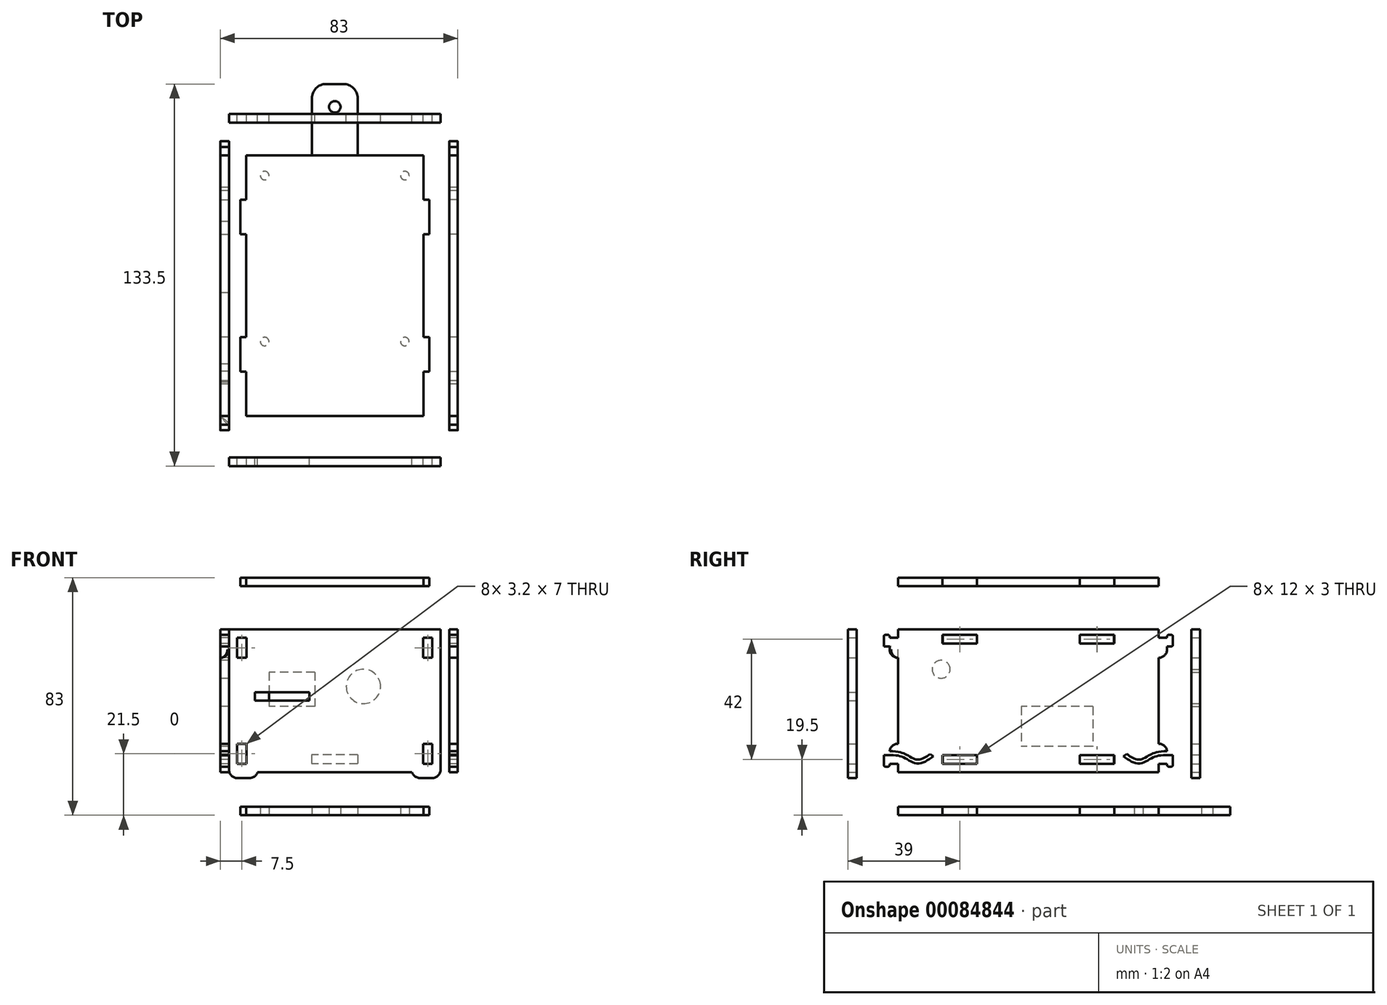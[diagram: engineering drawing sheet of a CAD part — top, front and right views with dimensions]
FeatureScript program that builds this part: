
annotation { "Feature Type Name" : "Feature", "Feature Type Description" : "" }
export const myFeature = defineFeature(function(context is Context, id is Id, definition is map)
    precondition{}
    {
        {
            var Q0;
            Q0=qCreatedBy(makeId("Top.planeOp"),FACE);
            cPlane(context, id + "F0", {"entities" : qUnion([Q0]), "cplaneType" : CPlaneType.OFFSET, "offset" : 40 * mm, "oppositeDirection" : true, "width" : 150 * mm, "height" : 150 * mm});
        }
        {
            var Q0;
            Q0=qCreatedBy(id+"F0.planeOp",FACE);
            var sketch = newSketch(context, id + "F1", { "sketchPlane" : qUnion([Q0])});
            skLineSegment(sketch, "E0", {"start": v(31, 45.5) * mm, "end": v(31, 30) * mm});
            skLineSegment(sketch, "E1", {"start": v(31, 30) * mm, "end": v(33, 30) * mm});
            skLineSegment(sketch, "E2", {"start": v(33, 30) * mm, "end": v(33, 18) * mm});
            skLineSegment(sketch, "E3", {"start": v(33, 18) * mm, "end": v(31, 18) * mm});
            skLineSegment(sketch, "E4", {"start": v(31, 18) * mm, "end": v(31, -18) * mm});
            skLineSegment(sketch, "E5", {"start": v(31, -18) * mm, "end": v(33, -18) * mm});
            skLineSegment(sketch, "E6", {"start": v(33, -18) * mm, "end": v(33, -30) * mm});
            skLineSegment(sketch, "E7", {"start": v(33, -30) * mm, "end": v(31, -30) * mm});
            skLineSegment(sketch, "E8", {"start": v(31, -30) * mm, "end": v(31, -45.5) * mm});
            skLineSegment(sketch, "E9", {"start": v(31, -45.5) * mm, "end": v(0, -45.5) * mm});
            skLineSegment(sketch, "E10", {"start": v(0, -45.5) * mm, "end": v(0, 45.5) * mm, "construction": true});
            skPoint(sketch, "E11", {"position": v(0, 0) * mm});
            skLineSegment(sketch, "E12.MirrorCS", {"start": v(-31, -18) * mm, "end": v(-33, -18) * mm});
            skLineSegment(sketch, "E13.MirrorCS", {"start": v(-33, -18) * mm, "end": v(-33, -30) * mm});
            skLineSegment(sketch, "E14.MirrorCS", {"start": v(-33, -30) * mm, "end": v(-31, -30) * mm});
            skLineSegment(sketch, "E15.MirrorCS", {"start": v(-31, -30) * mm, "end": v(-31, -45.5) * mm});
            skLineSegment(sketch, "E16.MirrorCS", {"start": v(-31, -45.5) * mm, "end": v(0, -45.5) * mm});
            skLineSegment(sketch, "E17.MirrorCS", {"start": v(-31, 18) * mm, "end": v(-31, -18) * mm});
            skLineSegment(sketch, "E18.MirrorCS", {"start": v(-33, 18) * mm, "end": v(-31, 18) * mm});
            skLineSegment(sketch, "E19.MirrorCS", {"start": v(-33, 30) * mm, "end": v(-33, 18) * mm});
            skLineSegment(sketch, "E20.MirrorCS", {"start": v(-31, 30) * mm, "end": v(-33, 30) * mm});
            skLineSegment(sketch, "E21.MirrorCS", {"start": v(-31, 45.5) * mm, "end": v(-31, 30) * mm});
            skCircle(sketch, "E22", {"center": v(24.5, 38.5) * mm, "radius": 1.5 * mm});
            skCircle(sketch, "E23.0.1.0", {"center": v(24.5, -19.5) * mm, "radius": 1.5 * mm});
            skCircle(sketch, "E23.1.0.0", {"center": v(-24.5, 38.5) * mm, "radius": 1.5 * mm});
            skCircle(sketch, "E23.1.1.0", {"center": v(-24.5, -19.5) * mm, "radius": 1.5 * mm});
            skLineSegment(sketch, "E23.direction1", {"start": v(24.5, 38.5) * mm, "end": v(-24.5, 38.5) * mm, "construction": true});
            skLineSegment(sketch, "E23.direction2", {"start": v(24.5, 38.5) * mm, "end": v(24.5, -19.5) * mm, "construction": true});
            skLineSegment(sketch, "E24", {"start": v(24.5, -19.5) * mm, "end": v(-24.5, -19.5) * mm, "construction": true});
            skPoint(sketch, "E25", {"position": v(0, -19.5) * mm});
            skLineSegment(sketch, "E26", {"start": v(31, 45.5) * mm, "end": v(8, 45.5) * mm});
            skLineSegment(sketch, "E27", {"start": v(8, 45.5) * mm, "end": v(8, 65.5) * mm});
            skLineSegment(sketch, "E28", {"start": v(3, 70.5) * mm, "end": v(0, 70.5) * mm});
            skLineSegment(sketch, "E29.MirrorCS", {"start": v(-31, 45.5) * mm, "end": v(-8, 45.5) * mm});
            skLineSegment(sketch, "E30.MirrorCS", {"start": v(-8, 45.5) * mm, "end": v(-8, 65.5) * mm});
            skLineSegment(sketch, "E31.MirrorCS", {"start": v(-3, 70.5) * mm, "end": v(0, 70.5) * mm});
            skCircle(sketch, "E32", {"center": v(0, 62.5) * mm, "radius": 2 * mm});
            skPoint(sketch, "E33.visualSharp", {"position": v(8, 70.5) * mm});
            skArc(sketch, "E33.filletArc", {"start": v(8, 65.5) * mm, "mid": v(6.54, 69.04) * mm, "end": v(3, 70.5) * mm});
            skPoint(sketch, "E34.visualSharp", {"position": v(-8, 70.5) * mm});
            skArc(sketch, "E34.filletArc", {"start": v(-3, 70.5) * mm, "mid": v(-6.54, 69.04) * mm, "end": v(-8, 65.5) * mm});
            skSolve(sketch);
        }
        {
            var Q0;
            Q0=qSketchRegion(id+"F1",true);
            extrude(context, id + "F2", {"entities" : qUnion([Q0]), "depth" : 3 * mm});
        }
        {
            var Q0;
            Q0=qCreatedBy(makeId("Top.planeOp"),FACE);
            cPlane(context, id + "F3", {"entities" : qUnion([Q0]), "cplaneType" : CPlaneType.OFFSET, "offset" : 40 * mm, "width" : 150 * mm, "height" : 150 * mm});
        }
        {
            var Q0;
            Q0=qCreatedBy(id+"F3.planeOp",FACE);
            var sketch = newSketch(context, id + "F4", { "sketchPlane" : qUnion([Q0])});
            skLineSegment(sketch, "E35", {"start": v(0, 45.5) * mm, "end": v(31, 45.5) * mm});
            skLineSegment(sketch, "E36", {"start": v(31, 45.5) * mm, "end": v(31, 30) * mm});
            skLineSegment(sketch, "E37", {"start": v(31, 30) * mm, "end": v(33, 30) * mm});
            skLineSegment(sketch, "E38", {"start": v(33, 30) * mm, "end": v(33, 18) * mm});
            skLineSegment(sketch, "E39", {"start": v(33, 18) * mm, "end": v(31, 18) * mm});
            skLineSegment(sketch, "E40", {"start": v(31, 18) * mm, "end": v(31, -18) * mm});
            skLineSegment(sketch, "E41", {"start": v(31, -18) * mm, "end": v(33, -18) * mm});
            skLineSegment(sketch, "E42", {"start": v(33, -18) * mm, "end": v(33, -30) * mm});
            skLineSegment(sketch, "E43", {"start": v(33, -30) * mm, "end": v(31, -30) * mm});
            skLineSegment(sketch, "E44", {"start": v(31, -30) * mm, "end": v(31, -45.5) * mm});
            skLineSegment(sketch, "E45", {"start": v(31, -45.5) * mm, "end": v(0, -45.5) * mm});
            skLineSegment(sketch, "E46.MirrorCS", {"start": v(-31, -18) * mm, "end": v(-33, -18) * mm});
            skLineSegment(sketch, "E47.MirrorCS", {"start": v(-33, -18) * mm, "end": v(-33, -30) * mm});
            skLineSegment(sketch, "E48.MirrorCS", {"start": v(-33, -30) * mm, "end": v(-31, -30) * mm});
            skLineSegment(sketch, "E49.MirrorCS", {"start": v(-31, -30) * mm, "end": v(-31, -45.5) * mm});
            skLineSegment(sketch, "E50.MirrorCS", {"start": v(-31, -45.5) * mm, "end": v(0, -45.5) * mm});
            skLineSegment(sketch, "E51.MirrorCS", {"start": v(-31, 18) * mm, "end": v(-31, -18) * mm});
            skLineSegment(sketch, "E52.MirrorCS", {"start": v(-33, 18) * mm, "end": v(-31, 18) * mm});
            skLineSegment(sketch, "E53.MirrorCS", {"start": v(-33, 30) * mm, "end": v(-33, 18) * mm});
            skLineSegment(sketch, "E54.MirrorCS", {"start": v(-31, 30) * mm, "end": v(-33, 30) * mm});
            skLineSegment(sketch, "E55.MirrorCS", {"start": v(-31, 45.5) * mm, "end": v(-31, 30) * mm});
            skLineSegment(sketch, "E56.MirrorCS", {"start": v(0, 45.5) * mm, "end": v(-31, 45.5) * mm});
            skLineSegment(sketch, "E57", {"start": v(0, 45.5) * mm, "end": v(0, -45.5) * mm, "construction": true});
            skPoint(sketch, "E58", {"position": v(0, 0) * mm});
            skSolve(sketch);
        }
        {
            var Q0;
            Q0=makeQuery(id+"F4.imprint","IMPRINT",FACE,{"disambiguationData":[TD([[makeQuery(id+"F4.imprint","IMPRINT",EDGE,{"derivedFrom":sQuery(id+"F4.wireOp",EDGE,"E35")}),-1.0]])]});
            extrude(context, id + "F5", {"entities" : qUnion([Q0]), "depth" : 3 * mm});
        }
        {
            var Q0;
            Q0=qCreatedBy(makeId("Right.planeOp"),FACE);
            cPlane(context, id + "F6", {"entities" : qUnion([Q0]), "cplaneType" : CPlaneType.OFFSET, "offset" : 40 * mm, "oppositeDirection" : true, "width" : 150 * mm, "height" : 150 * mm});
        }
        {
            var Q0;
            Q0=qCreatedBy(id+"F6.planeOp",FACE);
            var sketch = newSketch(context, id + "F7", { "sketchPlane" : qUnion([Q0])});
            skLineSegment(sketch, "E59.MirrorCS", {"start": v(-48.5, 23) * mm, "end": v(-48.5, 22) * mm});
            skLineSegment(sketch, "E60.MirrorCS", {"start": v(-48.5, -17.6) * mm, "end": v(-48.5, -15) * mm});
            skLineSegment(sketch, "E61.MirrorCS", {"start": v(-48.5, -22) * mm, "end": v(-48.5, -23) * mm});
            skLineSegment(sketch, "E62.MirrorCS", {"start": v(-48.5, -23) * mm, "end": v(-50.5, -23) * mm});
            skLineSegment(sketch, "E63.MirrorCS", {"start": v(-50.5, -23) * mm, "end": v(-50.5, -19) * mm});
            skLineSegment(sketch, "E64.MirrorCS", {"start": v(-48.5, -17.6) * mm, "end": v(-48.5, -22) * mm, "construction": true});
            skLineSegment(sketch, "E65.MirrorCS", {"start": v(-50.5, 23) * mm, "end": v(-48.5, 23) * mm});
            skLineSegment(sketch, "E66.MirrorCS", {"start": v(-33.23, -19.42) * mm, "end": v(-34.37, -18.6) * mm});
            skLineSegment(sketch, "E67.MirrorCS", {"start": v(-48.5, -17.6) * mm, "end": v(-48.65, -17.6) * mm});
            skLineSegment(sketch, "E68.MirrorCS", {"start": v(-45.5, 22) * mm, "end": v(-45.5, 25) * mm});
            skLineSegment(sketch, "E69.MirrorCS", {"start": v(-45.5, -22) * mm, "end": v(-48.5, -22) * mm});
            skLineSegment(sketch, "E70.MirrorCS", {"start": v(-48.5, -15) * mm, "end": v(-45.5, -15) * mm});
            skLineSegment(sketch, "E71.MirrorCS", {"start": v(-45.5, -25) * mm, "end": v(-45.5, -22) * mm});
            skLineSegment(sketch, "E72.MirrorCS", {"start": v(-17.9, -19) * mm, "end": v(-17.9, -22) * mm});
            skLineSegment(sketch, "E73.MirrorCS", {"start": v(-48.5, 22) * mm, "end": v(-45.5, 22) * mm});
            skLineSegment(sketch, "E74.MirrorCS", {"start": v(-48.5, 19) * mm, "end": v(-48.5, 15) * mm});
            skLineSegment(sketch, "E75.MirrorCS", {"start": v(-48.5, 15) * mm, "end": v(-45.5, 15) * mm});
            skLineSegment(sketch, "E76.MirrorCS", {"start": v(-29.9, -19) * mm, "end": v(-29.9, -22) * mm});
            skLineSegment(sketch, "E77.MirrorCS", {"start": v(-48.5, 19) * mm, "end": v(-50.5, 19) * mm});
            skLineSegment(sketch, "E78.MirrorCS", {"start": v(-50.5, 19) * mm, "end": v(-50.5, 23) * mm});
            skFitSpline(sketch, "E79.MirrorCS", {"points": [v(-52.36, -17.56) * mm, v(-51.07, -17.58) * mm, v(-49.38, -17.58) * mm, v(-47.44, -17.63) * mm, v(-46.09, -17.74) * mm, v(-45.02, -17.93) * mm, v(-44.18, -18.16) * mm, v(-43.67, -18.34) * mm, v(-43.26, -18.51) * mm, v(-42.87, -18.7) * mm, v(-42.4, -18.94) * mm, v(-41.88, -19.24) * mm, v(-41.2, -19.63) * mm, v(-40.59, -19.98) * mm, v(-40.01, -20.25) * mm, v(-39.61, -20.4) * mm, v(-39.3, -20.5) * mm, v(-39.06, -20.54) * mm, v(-38.9, -20.55) * mm, v(-38.72, -20.56) * mm, v(-38.47, -20.55) * mm, v(-38.14, -20.5) * mm, v(-37.7, -20.4) * mm, v(-37.1, -20.2) * mm, v(-36.3, -19.82) * mm, v(-35.31, -19.24) * mm, v(-34.68, -18.82) * mm, v(-34.37, -18.6) * mm]});
            skFitSpline(sketch, "E80.MirrorCS", {"points": [v(-50.5, -19) * mm, v(-43.39, -19.86) * mm, v(-38.75, -21.96) * mm, v(-33.23, -19.42) * mm], "startDerivative": vector(31.3, 0.22) * mm, "endDerivative": vector(15, 10.88) * mm});
            skLineSegment(sketch, "E81.MirrorCS", {"start": v(-17.9, -19) * mm, "end": v(-29.9, -19) * mm});
            skLineSegment(sketch, "E82.MirrorCS", {"start": v(-17.9, -22) * mm, "end": v(-29.9, -22) * mm});
            skLineSegment(sketch, "E83.MirrorCS", {"start": v(-45.5, 25) * mm, "end": v(0, 25) * mm});
            skPoint(sketch, "E84.MirrorP", {"position": v(-48.5, -17.6) * mm});
            skLineSegment(sketch, "E85.MirrorCS", {"start": v(-45.5, -15) * mm, "end": v(-45.5, 15) * mm});
            skLineSegment(sketch, "E86.MirrorCS", {"start": v(-45.5, -25) * mm, "end": v(0, -25) * mm});
            skLineSegment(sketch, "E87.MirrorCS", {"start": v(0, 25) * mm, "end": v(0, -25) * mm, "construction": true});
            skPoint(sketch, "E88.MirrorP", {"position": v(-48.65, -17.6) * mm});
            skPoint(sketch, "E89", {"position": v(0, 0) * mm});
            skLineSegment(sketch, "E90.MirrorCS", {"start": v(-17.9, 20) * mm, "end": v(-29.9, 20) * mm});
            skLineSegment(sketch, "E91.MirrorCS", {"start": v(-17.9, 23) * mm, "end": v(-29.9, 23) * mm});
            skLineSegment(sketch, "E92.MirrorCS", {"start": v(-29.9, 20) * mm, "end": v(-29.9, 23) * mm});
            skLineSegment(sketch, "E93.MirrorCS", {"start": v(-17.9, 20) * mm, "end": v(-17.9, 23) * mm});
            skLineSegment(sketch, "E94", {"start": v(-45.5, -15) * mm, "end": v(-45.5, -22) * mm, "construction": true});
            skLineSegment(sketch, "E95.MirrorCS", {"start": v(48.5, -17.6) * mm, "end": v(48.65, -17.6) * mm});
            skLineSegment(sketch, "E96.MirrorCS", {"start": v(33.23, -19.42) * mm, "end": v(34.37, -18.6) * mm});
            skLineSegment(sketch, "E97.MirrorCS", {"start": v(48.5, -23) * mm, "end": v(50.5, -23) * mm});
            skLineSegment(sketch, "E98.MirrorCS", {"start": v(48.5, -22) * mm, "end": v(48.5, -23) * mm});
            skLineSegment(sketch, "E99.MirrorCS", {"start": v(48.5, -17.6) * mm, "end": v(48.5, -22) * mm, "construction": true});
            skLineSegment(sketch, "E100.MirrorCS", {"start": v(50.5, 23) * mm, "end": v(48.5, 23) * mm});
            skLineSegment(sketch, "E101.MirrorCS", {"start": v(45.5, -22) * mm, "end": v(48.5, -22) * mm});
            skLineSegment(sketch, "E102.MirrorCS", {"start": v(48.5, 23) * mm, "end": v(48.5, 22) * mm});
            skLineSegment(sketch, "E103.MirrorCS", {"start": v(50.5, -23) * mm, "end": v(50.5, -19) * mm});
            skLineSegment(sketch, "E104.MirrorCS", {"start": v(48.5, -15) * mm, "end": v(45.5, -15) * mm});
            skLineSegment(sketch, "E105.MirrorCS", {"start": v(45.5, -25) * mm, "end": v(45.5, -22) * mm});
            skLineSegment(sketch, "E106.MirrorCS", {"start": v(45.5, -15) * mm, "end": v(45.5, -22) * mm, "construction": true});
            skLineSegment(sketch, "E107.MirrorCS", {"start": v(45.5, 22) * mm, "end": v(45.5, 25) * mm});
            skLineSegment(sketch, "E108.MirrorCS", {"start": v(48.5, 19) * mm, "end": v(50.5, 19) * mm});
            skLineSegment(sketch, "E109.MirrorCS", {"start": v(50.5, 19) * mm, "end": v(50.5, 23) * mm});
            skLineSegment(sketch, "E110.MirrorCS", {"start": v(48.5, 15) * mm, "end": v(45.5, 15) * mm});
            skLineSegment(sketch, "E111.MirrorCS", {"start": v(17.9, 20) * mm, "end": v(17.9, 23) * mm});
            skLineSegment(sketch, "E112.MirrorCS", {"start": v(48.5, -17.6) * mm, "end": v(48.5, -15) * mm});
            skLineSegment(sketch, "E113.MirrorCS", {"start": v(17.9, -19) * mm, "end": v(17.9, -22) * mm});
            skLineSegment(sketch, "E114.MirrorCS", {"start": v(48.5, 22) * mm, "end": v(45.5, 22) * mm});
            skLineSegment(sketch, "E115.MirrorCS", {"start": v(29.9, 20) * mm, "end": v(29.9, 23) * mm});
            skLineSegment(sketch, "E116.MirrorCS", {"start": v(29.9, -19) * mm, "end": v(29.9, -22) * mm});
            skPoint(sketch, "E117.MirrorP", {"position": v(48.65, -17.6) * mm});
            skFitSpline(sketch, "E118.MirrorCS", {"points": [v(50.5, -19) * mm, v(43.39, -19.86) * mm, v(38.75, -21.96) * mm, v(33.23, -19.42) * mm], "startDerivative": vector(-31.3, 0.22) * mm, "endDerivative": vector(-15, 10.88) * mm});
            skLineSegment(sketch, "E119.MirrorCS", {"start": v(17.9, 20) * mm, "end": v(29.9, 20) * mm});
            skLineSegment(sketch, "E120.MirrorCS", {"start": v(45.5, 25) * mm, "end": v(0, 25) * mm});
            skLineSegment(sketch, "E121.MirrorCS", {"start": v(45.5, -15) * mm, "end": v(45.5, 15) * mm});
            skLineSegment(sketch, "E122.MirrorCS", {"start": v(17.9, -22) * mm, "end": v(29.9, -22) * mm});
            skLineSegment(sketch, "E123.MirrorCS", {"start": v(45.5, -25) * mm, "end": v(0, -25) * mm});
            skLineSegment(sketch, "E124.MirrorCS", {"start": v(17.9, -19) * mm, "end": v(29.9, -19) * mm});
            skLineSegment(sketch, "E125.MirrorCS", {"start": v(17.9, 23) * mm, "end": v(29.9, 23) * mm});
            skFitSpline(sketch, "E126.MirrorCS", {"points": [v(52.36, -17.56) * mm, v(51.07, -17.58) * mm, v(49.38, -17.58) * mm, v(47.44, -17.63) * mm, v(46.09, -17.74) * mm, v(45.02, -17.93) * mm, v(44.18, -18.16) * mm, v(43.67, -18.34) * mm, v(43.26, -18.51) * mm, v(42.87, -18.7) * mm, v(42.4, -18.94) * mm, v(41.88, -19.24) * mm, v(41.2, -19.63) * mm, v(40.59, -19.98) * mm, v(40.01, -20.25) * mm, v(39.61, -20.4) * mm, v(39.3, -20.5) * mm, v(39.06, -20.54) * mm, v(38.9, -20.55) * mm, v(38.72, -20.56) * mm, v(38.47, -20.55) * mm, v(38.14, -20.5) * mm, v(37.7, -20.4) * mm, v(37.1, -20.2) * mm, v(36.3, -19.82) * mm, v(35.31, -19.24) * mm, v(34.68, -18.82) * mm, v(34.37, -18.6) * mm]});
            skPoint(sketch, "E127.MirrorP", {"position": v(48.5, -17.6) * mm});
            skLineSegment(sketch, "E128.MirrorCS", {"start": v(48.5, 19) * mm, "end": v(48.5, 15) * mm});
            skLineSegment(sketch, "E129", {"start": v(38.75, -21.96) * mm, "end": v(38.75, -20.56) * mm, "construction": true});
            skLineSegment(sketch, "E130", {"start": v(43.39, -19.86) * mm, "end": v(43.39, -18.46) * mm, "construction": true});
            skLineSegment(sketch, "E131.bottom", {"start": v(22.5, -2) * mm, "end": v(-2.5, -2) * mm});
            skLineSegment(sketch, "E131.top", {"start": v(22.5, -16) * mm, "end": v(-2.5, -16) * mm});
            skLineSegment(sketch, "E131.left", {"start": v(22.5, -2) * mm, "end": v(22.5, -16) * mm});
            skLineSegment(sketch, "E131.right", {"start": v(-2.5, -2) * mm, "end": v(-2.5, -16) * mm});
            skCircle(sketch, "E132", {"center": v(-30.5, 11) * mm, "radius": 3.15 * mm});
            skLineSegment(sketch, "E133", {"start": v(-17.9, 20) * mm, "end": v(-17.9, -19) * mm, "construction": true});
            skSolve(sketch);
        }
        {
            var Q0;
            Q0=qSketchRegion(id+"F7",true);
            extrude(context, id + "F8", {"entities" : qUnion([Q0]), "depth" : 3 * mm});
        }
        {
            var Q0;
            Q0=qCreatedBy(makeId("Right.planeOp"),FACE);
            cPlane(context, id + "F9", {"entities" : qUnion([Q0]), "cplaneType" : CPlaneType.OFFSET, "offset" : 40 * mm, "width" : 150 * mm, "height" : 150 * mm});
        }
        {
            var Q0;
            Q0=qCreatedBy(id+"F9.planeOp",FACE);
            var sketch = newSketch(context, id + "F10", { "sketchPlane" : qUnion([Q0])});
            skLineSegment(sketch, "E134.MirrorCS", {"start": v(-48.5, 23) * mm, "end": v(-48.5, 22) * mm});
            skLineSegment(sketch, "E135.MirrorCS", {"start": v(-48.5, -17.6) * mm, "end": v(-48.5, -15) * mm});
            skLineSegment(sketch, "E136.MirrorCS", {"start": v(-48.5, -22) * mm, "end": v(-48.5, -23) * mm});
            skLineSegment(sketch, "E137.MirrorCS", {"start": v(-48.5, -23) * mm, "end": v(-50.5, -23) * mm});
            skLineSegment(sketch, "E138.MirrorCS", {"start": v(-50.5, -23) * mm, "end": v(-50.5, -19) * mm});
            skLineSegment(sketch, "E139.MirrorCS", {"start": v(-48.5, -17.6) * mm, "end": v(-48.5, -22) * mm, "construction": true});
            skLineSegment(sketch, "E140.MirrorCS", {"start": v(-50.5, 23) * mm, "end": v(-48.5, 23) * mm});
            skLineSegment(sketch, "E141.MirrorCS", {"start": v(-33.23, -19.42) * mm, "end": v(-34.37, -18.6) * mm});
            skLineSegment(sketch, "E142.MirrorCS", {"start": v(-48.5, -17.6) * mm, "end": v(-48.65, -17.6) * mm});
            skLineSegment(sketch, "E143.MirrorCS", {"start": v(-45.5, 22) * mm, "end": v(-45.5, 25) * mm});
            skLineSegment(sketch, "E144.MirrorCS", {"start": v(-45.5, -22) * mm, "end": v(-48.5, -22) * mm});
            skLineSegment(sketch, "E145.MirrorCS", {"start": v(-48.5, -15) * mm, "end": v(-45.5, -15) * mm});
            skLineSegment(sketch, "E146.MirrorCS", {"start": v(-45.5, -25) * mm, "end": v(-45.5, -22) * mm});
            skLineSegment(sketch, "E147.MirrorCS", {"start": v(-18, -19) * mm, "end": v(-18, -22) * mm});
            skLineSegment(sketch, "E148.MirrorCS", {"start": v(-48.5, 22) * mm, "end": v(-45.5, 22) * mm});
            skLineSegment(sketch, "E149.MirrorCS", {"start": v(-48.5, 19) * mm, "end": v(-48.5, 15) * mm});
            skLineSegment(sketch, "E150.MirrorCS", {"start": v(-48.5, 15) * mm, "end": v(-45.5, 15) * mm});
            skLineSegment(sketch, "E151.MirrorCS", {"start": v(-30, -19) * mm, "end": v(-30, -22) * mm});
            skLineSegment(sketch, "E152.MirrorCS", {"start": v(-48.5, 19) * mm, "end": v(-50.5, 19) * mm});
            skLineSegment(sketch, "E153.MirrorCS", {"start": v(-50.5, 19) * mm, "end": v(-50.5, 23) * mm});
            skFitSpline(sketch, "E154.MirrorCS", {"points": [v(-52.36, -17.56) * mm, v(-51.07, -17.58) * mm, v(-49.38, -17.58) * mm, v(-47.44, -17.63) * mm, v(-46.09, -17.74) * mm, v(-45.02, -17.93) * mm, v(-44.18, -18.16) * mm, v(-43.67, -18.34) * mm, v(-43.26, -18.51) * mm, v(-42.87, -18.7) * mm, v(-42.4, -18.94) * mm, v(-41.88, -19.24) * mm, v(-41.2, -19.63) * mm, v(-40.59, -19.98) * mm, v(-40.01, -20.25) * mm, v(-39.61, -20.4) * mm, v(-39.3, -20.5) * mm, v(-39.06, -20.54) * mm, v(-38.9, -20.55) * mm, v(-38.72, -20.56) * mm, v(-38.47, -20.55) * mm, v(-38.14, -20.5) * mm, v(-37.7, -20.4) * mm, v(-37.1, -20.2) * mm, v(-36.3, -19.82) * mm, v(-35.31, -19.24) * mm, v(-34.68, -18.82) * mm, v(-34.37, -18.6) * mm]});
            skFitSpline(sketch, "E155.MirrorCS", {"points": [v(-50.5, -19) * mm, v(-43.39, -19.86) * mm, v(-38.75, -21.96) * mm, v(-33.23, -19.42) * mm], "startDerivative": vector(31.3, 0.22) * mm, "endDerivative": vector(15, 10.88) * mm});
            skLineSegment(sketch, "E156.MirrorCS", {"start": v(-18, -19) * mm, "end": v(-30, -19) * mm});
            skLineSegment(sketch, "E157.MirrorCS", {"start": v(-18, -22) * mm, "end": v(-30, -22) * mm});
            skLineSegment(sketch, "E158.MirrorCS", {"start": v(-45.5, 25) * mm, "end": v(0, 25) * mm});
            skPoint(sketch, "E159.MirrorP", {"position": v(-48.5, -17.6) * mm});
            skLineSegment(sketch, "E160.MirrorCS", {"start": v(-45.5, -15) * mm, "end": v(-45.5, 15) * mm});
            skLineSegment(sketch, "E161.MirrorCS", {"start": v(-45.5, -25) * mm, "end": v(0, -25) * mm});
            skLineSegment(sketch, "E162.MirrorCS", {"start": v(0, 25) * mm, "end": v(0, -25) * mm, "construction": true});
            skPoint(sketch, "E163.MirrorP", {"position": v(-48.65, -17.6) * mm});
            skPoint(sketch, "E164", {"position": v(0, 0) * mm});
            skLineSegment(sketch, "E165.MirrorCS", {"start": v(-18, 20) * mm, "end": v(-30, 20) * mm});
            skLineSegment(sketch, "E166.MirrorCS", {"start": v(-18, 23) * mm, "end": v(-30, 23) * mm});
            skLineSegment(sketch, "E167.MirrorCS", {"start": v(-30, 20) * mm, "end": v(-30, 23) * mm});
            skLineSegment(sketch, "E168.MirrorCS", {"start": v(-18, 20) * mm, "end": v(-18, 23) * mm});
            skLineSegment(sketch, "E169", {"start": v(-45.5, -15) * mm, "end": v(-45.5, -22) * mm, "construction": true});
            skLineSegment(sketch, "E170.MirrorCS", {"start": v(48.5, -17.6) * mm, "end": v(48.65, -17.6) * mm});
            skLineSegment(sketch, "E171.MirrorCS", {"start": v(33.23, -19.42) * mm, "end": v(34.37, -18.6) * mm});
            skLineSegment(sketch, "E172.MirrorCS", {"start": v(48.5, -23) * mm, "end": v(50.5, -23) * mm});
            skLineSegment(sketch, "E173.MirrorCS", {"start": v(48.5, -22) * mm, "end": v(48.5, -23) * mm});
            skLineSegment(sketch, "E174.MirrorCS", {"start": v(48.5, -17.6) * mm, "end": v(48.5, -22) * mm, "construction": true});
            skLineSegment(sketch, "E175.MirrorCS", {"start": v(50.5, 23) * mm, "end": v(48.5, 23) * mm});
            skLineSegment(sketch, "E176.MirrorCS", {"start": v(45.5, -22) * mm, "end": v(48.5, -22) * mm});
            skLineSegment(sketch, "E177.MirrorCS", {"start": v(48.5, 23) * mm, "end": v(48.5, 22) * mm});
            skLineSegment(sketch, "E178.MirrorCS", {"start": v(50.5, -23) * mm, "end": v(50.5, -19) * mm});
            skLineSegment(sketch, "E179.MirrorCS", {"start": v(48.5, -15) * mm, "end": v(45.5, -15) * mm});
            skLineSegment(sketch, "E180.MirrorCS", {"start": v(45.5, -25) * mm, "end": v(45.5, -22) * mm});
            skLineSegment(sketch, "E181.MirrorCS", {"start": v(45.5, -15) * mm, "end": v(45.5, -22) * mm, "construction": true});
            skLineSegment(sketch, "E182.MirrorCS", {"start": v(45.5, 22) * mm, "end": v(45.5, 25) * mm});
            skLineSegment(sketch, "E183.MirrorCS", {"start": v(48.5, 19) * mm, "end": v(50.5, 19) * mm});
            skLineSegment(sketch, "E184.MirrorCS", {"start": v(50.5, 19) * mm, "end": v(50.5, 23) * mm});
            skLineSegment(sketch, "E185.MirrorCS", {"start": v(48.5, 15) * mm, "end": v(45.5, 15) * mm});
            skLineSegment(sketch, "E186.MirrorCS", {"start": v(18, 20) * mm, "end": v(18, 23) * mm});
            skLineSegment(sketch, "E187.MirrorCS", {"start": v(48.5, -17.6) * mm, "end": v(48.5, -15) * mm});
            skLineSegment(sketch, "E188.MirrorCS", {"start": v(18, -19) * mm, "end": v(18, -22) * mm});
            skLineSegment(sketch, "E189.MirrorCS", {"start": v(48.5, 22) * mm, "end": v(45.5, 22) * mm});
            skLineSegment(sketch, "E190.MirrorCS", {"start": v(30, 20) * mm, "end": v(30, 23) * mm});
            skLineSegment(sketch, "E191.MirrorCS", {"start": v(30, -19) * mm, "end": v(30, -22) * mm});
            skPoint(sketch, "E192.MirrorP", {"position": v(48.65, -17.6) * mm});
            skFitSpline(sketch, "E193.MirrorCS", {"points": [v(50.5, -19) * mm, v(43.39, -19.86) * mm, v(38.75, -21.96) * mm, v(33.23, -19.42) * mm], "startDerivative": vector(-31.3, 0.22) * mm, "endDerivative": vector(-15, 10.88) * mm});
            skLineSegment(sketch, "E194.MirrorCS", {"start": v(18, 20) * mm, "end": v(30, 20) * mm});
            skLineSegment(sketch, "E195.MirrorCS", {"start": v(45.5, 25) * mm, "end": v(0, 25) * mm});
            skLineSegment(sketch, "E196.MirrorCS", {"start": v(45.5, -15) * mm, "end": v(45.5, 15) * mm});
            skLineSegment(sketch, "E197.MirrorCS", {"start": v(18, -22) * mm, "end": v(30, -22) * mm});
            skLineSegment(sketch, "E198.MirrorCS", {"start": v(45.5, -25) * mm, "end": v(0, -25) * mm});
            skLineSegment(sketch, "E199.MirrorCS", {"start": v(18, -19) * mm, "end": v(30, -19) * mm});
            skLineSegment(sketch, "E200.MirrorCS", {"start": v(18, 23) * mm, "end": v(30, 23) * mm});
            skFitSpline(sketch, "E201.MirrorCS", {"points": [v(52.36, -17.56) * mm, v(51.07, -17.58) * mm, v(49.38, -17.58) * mm, v(47.44, -17.63) * mm, v(46.09, -17.74) * mm, v(45.02, -17.93) * mm, v(44.18, -18.16) * mm, v(43.67, -18.34) * mm, v(43.26, -18.51) * mm, v(42.87, -18.7) * mm, v(42.4, -18.94) * mm, v(41.88, -19.24) * mm, v(41.2, -19.63) * mm, v(40.59, -19.98) * mm, v(40.01, -20.25) * mm, v(39.61, -20.4) * mm, v(39.3, -20.5) * mm, v(39.06, -20.54) * mm, v(38.9, -20.55) * mm, v(38.72, -20.56) * mm, v(38.47, -20.55) * mm, v(38.14, -20.5) * mm, v(37.7, -20.4) * mm, v(37.1, -20.2) * mm, v(36.3, -19.82) * mm, v(35.31, -19.24) * mm, v(34.68, -18.82) * mm, v(34.37, -18.6) * mm]});
            skPoint(sketch, "E202.MirrorP", {"position": v(48.5, -17.6) * mm});
            skLineSegment(sketch, "E203.MirrorCS", {"start": v(48.5, 19) * mm, "end": v(48.5, 15) * mm});
            skLineSegment(sketch, "E204", {"start": v(38.75, -21.96) * mm, "end": v(38.75, -20.56) * mm, "construction": true});
            skLineSegment(sketch, "E205", {"start": v(43.39, -19.86) * mm, "end": v(43.39, -18.46) * mm, "construction": true});
            skSolve(sketch);
        }
        {
            var Q0;
            Q0=qSketchRegion(id+"F10",true);
            extrude(context, id + "F11", {"entities" : qUnion([Q0]), "depth" : 3 * mm});
        }
        {
            var Q0;
            Q0=makeQuery(id+"F8.opExtrude","SWEPT_EDGE",EDGE,{"disambiguationData":[OSD([sQuery(id+"F7.wireOp",EDGE,"E59.MirrorCS"),sQuery(id+"F7.wireOp",EDGE,"E65.MirrorCS")])]});
            var Q1;
            Q1=makeQuery(id+"F8.opExtrude","SWEPT_EDGE",EDGE,{"disambiguationData":[OSD([sQuery(id+"F7.wireOp",EDGE,"E65.MirrorCS"),sQuery(id+"F7.wireOp",EDGE,"E78.MirrorCS")])]});
            var Q2;
            Q2=makeQuery(id+"F11.opExtrude","SWEPT_EDGE",EDGE,{"disambiguationData":[OSD([sQuery(id+"F10.wireOp",EDGE,"E134.MirrorCS"),sQuery(id+"F10.wireOp",EDGE,"E140.MirrorCS")])]});
            var Q3;
            Q3=makeQuery(id+"F11.opExtrude","SWEPT_EDGE",EDGE,{"disambiguationData":[OSD([sQuery(id+"F10.wireOp",EDGE,"E140.MirrorCS"),sQuery(id+"F10.wireOp",EDGE,"E153.MirrorCS")])]});
            var Q4;
            Q4=makeQuery(id+"F11.opExtrude","SWEPT_EDGE",EDGE,{"disambiguationData":[OSD([sQuery(id+"F10.wireOp",EDGE,"E152.MirrorCS"),sQuery(id+"F10.wireOp",EDGE,"E153.MirrorCS")])]});
            var Q5;
            Q5=makeQuery(id+"F8.opExtrude","CAP_EDGE",EDGE,{"disambiguationData":[OSD([sQuery(id+"F7.wireOp",EDGE,"E74.MirrorCS")])],"isStart":false});
            var Q6;
            Q6=makeQuery(id+"F11.opExtrude","SWEPT_EDGE",EDGE,{"disambiguationData":[OSD([sQuery(id+"F10.wireOp",EDGE,"E137.MirrorCS"),sQuery(id+"F10.wireOp",EDGE,"E138.MirrorCS")])]});
            var Q7;
            Q7=makeQuery(id+"F11.opExtrude","SWEPT_EDGE",EDGE,{"disambiguationData":[OSD([sQuery(id+"F10.wireOp",EDGE,"E136.MirrorCS"),sQuery(id+"F10.wireOp",EDGE,"E137.MirrorCS")])]});
            var Q8;
            Q8=makeQuery(id+"F8.opExtrude","SWEPT_EDGE",EDGE,{"disambiguationData":[OSD([sQuery(id+"F7.wireOp",EDGE,"E62.MirrorCS"),sQuery(id+"F7.wireOp",EDGE,"E63.MirrorCS")])]});
            var Q9;
            Q9=makeQuery(id+"F8.opExtrude","SWEPT_EDGE",EDGE,{"disambiguationData":[OSD([sQuery(id+"F7.wireOp",EDGE,"E61.MirrorCS"),sQuery(id+"F7.wireOp",EDGE,"E62.MirrorCS")])]});
            var Q10;
            Q10=makeQuery(id+"F8.opExtrude","SWEPT_EDGE",EDGE,{"disambiguationData":[OSD([sQuery(id+"F7.wireOp",EDGE,"E97.MirrorCS"),sQuery(id+"F7.wireOp",EDGE,"E98.MirrorCS")])]});
            var Q11;
            Q11=makeQuery(id+"F8.opExtrude","SWEPT_EDGE",EDGE,{"disambiguationData":[OSD([sQuery(id+"F7.wireOp",EDGE,"E97.MirrorCS"),sQuery(id+"F7.wireOp",EDGE,"E103.MirrorCS")])]});
            var Q12;
            Q12=makeQuery(id+"F11.opExtrude","SWEPT_EDGE",EDGE,{"disambiguationData":[OSD([sQuery(id+"F10.wireOp",EDGE,"E172.MirrorCS"),sQuery(id+"F10.wireOp",EDGE,"E173.MirrorCS")])]});
            var Q13;
            Q13=makeQuery(id+"F11.opExtrude","SWEPT_EDGE",EDGE,{"disambiguationData":[OSD([sQuery(id+"F10.wireOp",EDGE,"E172.MirrorCS"),sQuery(id+"F10.wireOp",EDGE,"E178.MirrorCS")])]});
            var Q14;
            Q14=makeQuery(id+"F8.opExtrude","SWEPT_EDGE",EDGE,{"disambiguationData":[OSD([sQuery(id+"F7.wireOp",EDGE,"E108.MirrorCS"),sQuery(id+"F7.wireOp",EDGE,"E109.MirrorCS")])]});
            var Q15;
            Q15=makeQuery(id+"F11.opExtrude","SWEPT_EDGE",EDGE,{"disambiguationData":[OSD([sQuery(id+"F10.wireOp",EDGE,"E183.MirrorCS"),sQuery(id+"F10.wireOp",EDGE,"E184.MirrorCS")])]});
            var Q16;
            Q16=makeQuery(id+"F8.opExtrude","SWEPT_EDGE",EDGE,{"disambiguationData":[OSD([sQuery(id+"F7.wireOp",EDGE,"E100.MirrorCS"),sQuery(id+"F7.wireOp",EDGE,"E109.MirrorCS")])]});
            var Q17;
            Q17=makeQuery(id+"F8.opExtrude","SWEPT_EDGE",EDGE,{"disambiguationData":[OSD([sQuery(id+"F7.wireOp",EDGE,"E100.MirrorCS"),sQuery(id+"F7.wireOp",EDGE,"E102.MirrorCS")])]});
            var Q18;
            Q18=makeQuery(id+"F11.opExtrude","SWEPT_EDGE",EDGE,{"disambiguationData":[OSD([sQuery(id+"F10.wireOp",EDGE,"E175.MirrorCS"),sQuery(id+"F10.wireOp",EDGE,"E184.MirrorCS")])]});
            var Q19;
            Q19=makeQuery(id+"F11.opExtrude","SWEPT_EDGE",EDGE,{"disambiguationData":[OSD([sQuery(id+"F10.wireOp",EDGE,"E175.MirrorCS"),sQuery(id+"F10.wireOp",EDGE,"E177.MirrorCS")])]});
            fillet(context, id + "F12", {"entities" : qUnion([Q0, Q1, Q2, Q3, Q4, Q5, Q6, Q7, Q8, Q9, Q10, Q11, Q12, Q13, Q14, Q15, Q16, Q17, Q18, Q19]), "radius" : 0.5 * mm, "tangentPropagation" : true, "allowEdgeOverflow" : false});
        }
        {
            var Q0;
            Q0=makeQuery(id+"F11.opExtrude","SWEPT_EDGE",EDGE,{"disambiguationData":[OSD([sQuery(id+"F10.wireOp",EDGE,"E179.MirrorCS"),sQuery(id+"F10.wireOp",EDGE,"E187.MirrorCS")])]});
            var Q1;
            Q1=makeQuery(id+"F11.opExtrude","SWEPT_EDGE",EDGE,{"disambiguationData":[OSD([sQuery(id+"F10.wireOp",EDGE,"E185.MirrorCS"),sQuery(id+"F10.wireOp",EDGE,"E203.MirrorCS")])]});
            var Q2;
            Q2=makeQuery(id+"F8.opExtrude","SWEPT_EDGE",EDGE,{"disambiguationData":[OSD([sQuery(id+"F7.wireOp",EDGE,"E110.MirrorCS"),sQuery(id+"F7.wireOp",EDGE,"E128.MirrorCS")])]});
            var Q3;
            Q3=makeQuery(id+"F8.opExtrude","SWEPT_EDGE",EDGE,{"disambiguationData":[OSD([sQuery(id+"F7.wireOp",EDGE,"E104.MirrorCS"),sQuery(id+"F7.wireOp",EDGE,"E112.MirrorCS")])]});
            var Q4;
            Q4=makeQuery(id+"F11.opExtrude","SWEPT_EDGE",EDGE,{"disambiguationData":[OSD([sQuery(id+"F10.wireOp",EDGE,"E135.MirrorCS"),sQuery(id+"F10.wireOp",EDGE,"E145.MirrorCS")])]});
            var Q5;
            Q5=makeQuery(id+"F11.opExtrude","SWEPT_EDGE",EDGE,{"disambiguationData":[OSD([sQuery(id+"F10.wireOp",EDGE,"E149.MirrorCS"),sQuery(id+"F10.wireOp",EDGE,"E150.MirrorCS")])]});
            var Q6;
            Q6=makeQuery(id+"F8.opExtrude","SWEPT_EDGE",EDGE,{"disambiguationData":[OSD([sQuery(id+"F7.wireOp",EDGE,"E60.MirrorCS"),sQuery(id+"F7.wireOp",EDGE,"E70.MirrorCS")])]});
            var Q7;
            Q7=makeQuery(id+"F8.opExtrude","SWEPT_EDGE",EDGE,{"disambiguationData":[OSD([sQuery(id+"F7.wireOp",EDGE,"E74.MirrorCS"),sQuery(id+"F7.wireOp",EDGE,"E75.MirrorCS")])]});
            fillet(context, id + "F13", {"entities" : qUnion([Q0, Q1, Q2, Q3, Q4, Q5, Q6, Q7]), "radius" : 3 * mm, "tangentPropagation" : true, "allowEdgeOverflow" : false});
        }
        {
            var Q0;
            Q0=qCreatedBy(makeId("Front.planeOp"),FACE);
            cPlane(context, id + "F14", {"entities" : qUnion([Q0]), "cplaneType" : CPlaneType.OFFSET, "offset" : 60 * mm, "oppositeDirection" : true, "width" : 150 * mm, "height" : 150 * mm});
        }
        {
            var Q0;
            Q0=qCreatedBy(id+"F14.planeOp",FACE);
            var sketch = newSketch(context, id + "F15", { "sketchPlane" : qUnion([Q0])});
            skLineSegment(sketch, "E206.bottom", {"start": v(0, 25) * mm, "end": v(-37, 25) * mm});
            skLineSegment(sketch, "E206.top", {"start": v(0, -25) * mm, "end": v(-37, -25) * mm});
            skLineSegment(sketch, "E206.left", {"start": v(0, 25) * mm, "end": v(0, -25) * mm, "construction": true});
            skLineSegment(sketch, "E206.right", {"start": v(-37, 25) * mm, "end": v(-37, -25) * mm});
            skLineSegment(sketch, "E207.bottom", {"start": v(-37, -25) * mm, "end": v(-27, -25) * mm});
            skLineSegment(sketch, "E207.top", {"start": v(-37, -27) * mm, "end": v(-27, -27) * mm});
            skLineSegment(sketch, "E207.left", {"start": v(-37, -25) * mm, "end": v(-37, -27) * mm});
            skLineSegment(sketch, "E207.right", {"start": v(-27, -25) * mm, "end": v(-27, -27) * mm});
            skPoint(sketch, "E208", {"position": v(0, 0) * mm});
            skLineSegment(sketch, "E209", {"start": v(0, 0) * mm, "end": v(-37, 0) * mm, "construction": true});
            skLineSegment(sketch, "E210.bottom", {"start": v(-30.9, -15) * mm, "end": v(-34.1, -15) * mm});
            skLineSegment(sketch, "E210.top", {"start": v(-30.9, -22) * mm, "end": v(-34.1, -22) * mm});
            skLineSegment(sketch, "E210.left", {"start": v(-30.9, -15) * mm, "end": v(-30.9, -22) * mm});
            skLineSegment(sketch, "E210.right", {"start": v(-34.1, -15) * mm, "end": v(-34.1, -22) * mm});
            skLineSegment(sketch, "E211.MirrorCS", {"start": v(-30.9, 22) * mm, "end": v(-34.1, 22) * mm});
            skLineSegment(sketch, "E212.MirrorCS", {"start": v(-30.9, 15) * mm, "end": v(-34.1, 15) * mm});
            skLineSegment(sketch, "E213.MirrorCS", {"start": v(-30.9, 15) * mm, "end": v(-30.9, 22) * mm});
            skLineSegment(sketch, "E214.MirrorCS", {"start": v(-34.1, 15) * mm, "end": v(-34.1, 22) * mm});
            skLineSegment(sketch, "E215.MirrorCS", {"start": v(30.9, -22) * mm, "end": v(34.1, -22) * mm});
            skLineSegment(sketch, "E216.MirrorCS", {"start": v(30.9, -15) * mm, "end": v(34.1, -15) * mm});
            skLineSegment(sketch, "E217.MirrorCS", {"start": v(30.9, 15) * mm, "end": v(34.1, 15) * mm});
            skLineSegment(sketch, "E218.MirrorCS", {"start": v(30.9, 22) * mm, "end": v(34.1, 22) * mm});
            skLineSegment(sketch, "E219.MirrorCS", {"start": v(0, -25) * mm, "end": v(37, -25) * mm});
            skLineSegment(sketch, "E220.MirrorCS", {"start": v(0, 25) * mm, "end": v(37, 25) * mm});
            skLineSegment(sketch, "E221.MirrorCS", {"start": v(30.9, 15) * mm, "end": v(30.9, 22) * mm});
            skLineSegment(sketch, "E222.MirrorCS", {"start": v(30.9, -15) * mm, "end": v(30.9, -22) * mm});
            skLineSegment(sketch, "E223.MirrorCS", {"start": v(37, -25) * mm, "end": v(27, -25) * mm});
            skLineSegment(sketch, "E224.MirrorCS", {"start": v(37, -27) * mm, "end": v(27, -27) * mm});
            skLineSegment(sketch, "E225.MirrorCS", {"start": v(37, -25) * mm, "end": v(37, -27) * mm});
            skLineSegment(sketch, "E226.MirrorCS", {"start": v(27, -25) * mm, "end": v(27, -27) * mm});
            skLineSegment(sketch, "E227.MirrorCS", {"start": v(0, 0) * mm, "end": v(37, 0) * mm, "construction": true});
            skLineSegment(sketch, "E228.MirrorCS", {"start": v(37, 25) * mm, "end": v(37, -25) * mm});
            skLineSegment(sketch, "E229.MirrorCS", {"start": v(34.1, -15) * mm, "end": v(34.1, -22) * mm});
            skLineSegment(sketch, "E230.MirrorCS", {"start": v(34.1, 15) * mm, "end": v(34.1, 22) * mm});
            skLineSegment(sketch, "E231.bottom", {"start": v(-7, 10) * mm, "end": v(-23, 10) * mm});
            skLineSegment(sketch, "E231.top", {"start": v(-7, -2) * mm, "end": v(-23, -2) * mm});
            skLineSegment(sketch, "E231.left", {"start": v(-7, 10) * mm, "end": v(-7, -2) * mm});
            skLineSegment(sketch, "E231.right", {"start": v(-23, 10) * mm, "end": v(-23, -2) * mm});
            skCircle(sketch, "E232", {"center": v(10, 5) * mm, "radius": 6 * mm});
            skLineSegment(sketch, "E233.rect.bottom", {"start": v(8.05, -18.9) * mm, "end": v(-8.05, -18.9) * mm});
            skLineSegment(sketch, "E233.rect.top", {"start": v(8.05, -22) * mm, "end": v(-8.05, -22) * mm});
            skLineSegment(sketch, "E233.rect.left", {"start": v(8.05, -18.9) * mm, "end": v(8.05, -22) * mm});
            skLineSegment(sketch, "E233.rect.right", {"start": v(-8.05, -18.9) * mm, "end": v(-8.05, -22) * mm});
            skPoint(sketch, "E233.rect.middle", {"position": v(0, -20.45) * mm});
            skSolve(sketch);
        }
        {
            var Q0;
            Q0=qSketchRegion(id+"F15",true);
            extrude(context, id + "F16", {"entities" : qUnion([Q0]), "depth" : 3 * mm});
        }
        {
            var Q0;
            Q0=qCreatedBy(makeId("Front.planeOp"),FACE);
            cPlane(context, id + "F17", {"entities" : qUnion([Q0]), "cplaneType" : CPlaneType.OFFSET, "offset" : 60 * mm, "width" : 150 * mm, "height" : 150 * mm});
        }
        {
            var Q0;
            Q0=qCreatedBy(id+"F17.planeOp",FACE);
            var sketch = newSketch(context, id + "F18", { "sketchPlane" : qUnion([Q0])});
            skLineSegment(sketch, "E234.bottom", {"start": v(0, 25) * mm, "end": v(-37, 25) * mm});
            skLineSegment(sketch, "E234.top", {"start": v(0, -25) * mm, "end": v(-37, -25) * mm});
            skLineSegment(sketch, "E234.left", {"start": v(0, 25) * mm, "end": v(0, -25) * mm, "construction": true});
            skLineSegment(sketch, "E234.right", {"start": v(-37, 25) * mm, "end": v(-37, -25) * mm});
            skLineSegment(sketch, "E235.bottom", {"start": v(-37, -25) * mm, "end": v(-27, -25) * mm});
            skLineSegment(sketch, "E235.top", {"start": v(-37, -27) * mm, "end": v(-27, -27) * mm});
            skLineSegment(sketch, "E235.left", {"start": v(-37, -25) * mm, "end": v(-37, -27) * mm});
            skLineSegment(sketch, "E235.right", {"start": v(-27, -25) * mm, "end": v(-27, -27) * mm});
            skPoint(sketch, "E236", {"position": v(0, 0) * mm});
            skLineSegment(sketch, "E237", {"start": v(0, 0) * mm, "end": v(-37, 0) * mm, "construction": true});
            skLineSegment(sketch, "E238.bottom", {"start": v(-30.9, -15) * mm, "end": v(-34.1, -15) * mm});
            skLineSegment(sketch, "E238.top", {"start": v(-30.9, -22) * mm, "end": v(-34.1, -22) * mm});
            skLineSegment(sketch, "E238.left", {"start": v(-30.9, -15) * mm, "end": v(-30.9, -22) * mm});
            skLineSegment(sketch, "E238.right", {"start": v(-34.1, -15) * mm, "end": v(-34.1, -22) * mm});
            skLineSegment(sketch, "E239.MirrorCS", {"start": v(-30.9, 22) * mm, "end": v(-34.1, 22) * mm});
            skLineSegment(sketch, "E240.MirrorCS", {"start": v(-30.9, 15) * mm, "end": v(-34.1, 15) * mm});
            skLineSegment(sketch, "E241.MirrorCS", {"start": v(-30.9, 15) * mm, "end": v(-30.9, 22) * mm});
            skLineSegment(sketch, "E242.MirrorCS", {"start": v(-34.1, 15) * mm, "end": v(-34.1, 22) * mm});
            skLineSegment(sketch, "E243.MirrorCS", {"start": v(30.9, -22) * mm, "end": v(34.1, -22) * mm});
            skLineSegment(sketch, "E244.MirrorCS", {"start": v(30.9, -15) * mm, "end": v(34.1, -15) * mm});
            skLineSegment(sketch, "E245.MirrorCS", {"start": v(30.9, 15) * mm, "end": v(34.1, 15) * mm});
            skLineSegment(sketch, "E246.MirrorCS", {"start": v(30.9, 22) * mm, "end": v(34.1, 22) * mm});
            skLineSegment(sketch, "E247.MirrorCS", {"start": v(0, -25) * mm, "end": v(37, -25) * mm});
            skLineSegment(sketch, "E248.MirrorCS", {"start": v(0, 25) * mm, "end": v(37, 25) * mm});
            skLineSegment(sketch, "E249.MirrorCS", {"start": v(30.9, 15) * mm, "end": v(30.9, 22) * mm});
            skLineSegment(sketch, "E250.MirrorCS", {"start": v(30.9, -15) * mm, "end": v(30.9, -22) * mm});
            skLineSegment(sketch, "E251.MirrorCS", {"start": v(37, -25) * mm, "end": v(27, -25) * mm});
            skLineSegment(sketch, "E252.MirrorCS", {"start": v(37, -27) * mm, "end": v(27, -27) * mm});
            skLineSegment(sketch, "E253.MirrorCS", {"start": v(37, -25) * mm, "end": v(37, -27) * mm});
            skLineSegment(sketch, "E254.MirrorCS", {"start": v(27, -25) * mm, "end": v(27, -27) * mm});
            skLineSegment(sketch, "E255.MirrorCS", {"start": v(0, 0) * mm, "end": v(37, 0) * mm, "construction": true});
            skLineSegment(sketch, "E256.MirrorCS", {"start": v(37, 25) * mm, "end": v(37, -25) * mm});
            skLineSegment(sketch, "E257.MirrorCS", {"start": v(34.1, -15) * mm, "end": v(34.1, -22) * mm});
            skLineSegment(sketch, "E258.MirrorCS", {"start": v(34.1, 15) * mm, "end": v(34.1, 22) * mm});
            skLineSegment(sketch, "E259.bottom", {"start": v(-27.9, 3) * mm, "end": v(-8.9, 3) * mm});
            skLineSegment(sketch, "E259.top", {"start": v(-27.9, 0) * mm, "end": v(-8.9, 0) * mm});
            skLineSegment(sketch, "E259.left", {"start": v(-27.9, 3) * mm, "end": v(-27.9, 0) * mm});
            skLineSegment(sketch, "E259.right", {"start": v(-8.9, 3) * mm, "end": v(-8.9, 0) * mm});
            skSolve(sketch);
        }
        {
            var Q0;
            Q0=qSketchRegion(id+"F18",true);
            extrude(context, id + "F19", {"entities" : qUnion([Q0]), "depth" : 3 * mm});
        }
        {
            var Q0;
            Q0=makeQuery(id+"F19.opExtrude","SWEPT_EDGE",EDGE,{"disambiguationData":[OSD([sQuery(id+"F18.wireOp",EDGE,"E252.MirrorCS"),sQuery(id+"F18.wireOp",EDGE,"E254.MirrorCS")])]});
            var Q1;
            Q1=makeQuery(id+"F19.opExtrude","SWEPT_EDGE",EDGE,{"disambiguationData":[OSD([sQuery(id+"F18.wireOp",EDGE,"E252.MirrorCS"),sQuery(id+"F18.wireOp",EDGE,"E253.MirrorCS")])]});
            var Q2;
            Q2=makeQuery(id+"F19.opExtrude","SWEPT_EDGE",EDGE,{"disambiguationData":[OSD([sQuery(id+"F18.wireOp",EDGE,"E235.top"),sQuery(id+"F18.wireOp",EDGE,"E235.right")])]});
            var Q3;
            Q3=makeQuery(id+"F19.opExtrude","SWEPT_EDGE",EDGE,{"disambiguationData":[OSD([sQuery(id+"F18.wireOp",EDGE,"E235.top"),sQuery(id+"F18.wireOp",EDGE,"E235.left")])]});
            var Q4;
            Q4=makeQuery(id+"F16.opExtrude","SWEPT_EDGE",EDGE,{"disambiguationData":[OSD([sQuery(id+"F15.wireOp",EDGE,"E224.MirrorCS"),sQuery(id+"F15.wireOp",EDGE,"E225.MirrorCS")])]});
            var Q5;
            Q5=makeQuery(id+"F16.opExtrude","SWEPT_EDGE",EDGE,{"disambiguationData":[OSD([sQuery(id+"F15.wireOp",EDGE,"E224.MirrorCS"),sQuery(id+"F15.wireOp",EDGE,"E226.MirrorCS")])]});
            var Q6;
            Q6=makeQuery(id+"F16.opExtrude","SWEPT_EDGE",EDGE,{"disambiguationData":[OSD([sQuery(id+"F15.wireOp",EDGE,"E207.top"),sQuery(id+"F15.wireOp",EDGE,"E207.right")])]});
            var Q7;
            Q7=makeQuery(id+"F16.opExtrude","SWEPT_EDGE",EDGE,{"disambiguationData":[OSD([sQuery(id+"F15.wireOp",EDGE,"E207.top"),sQuery(id+"F15.wireOp",EDGE,"E207.left")])]});
            fillet(context, id + "F20", {"entities" : qUnion([Q0, Q1, Q2, Q3, Q4, Q5, Q6, Q7]), "radius" : 3 * mm, "tangentPropagation" : true, "allowEdgeOverflow" : false});
        }
    });
